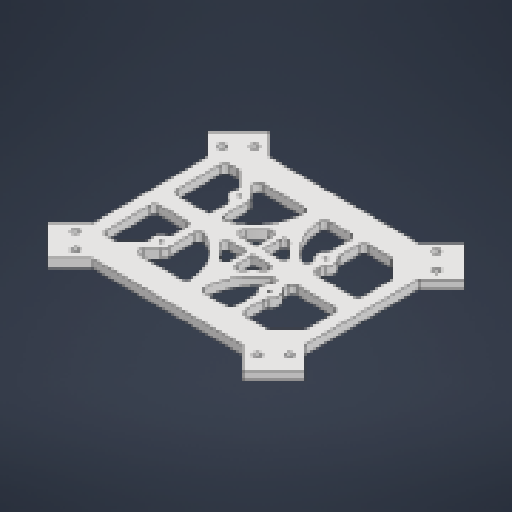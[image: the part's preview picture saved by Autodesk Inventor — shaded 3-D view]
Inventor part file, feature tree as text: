
AUTODESK INVENTOR PART (.ipt)
format: ipt  version: 2023 (Build 270158000, 158)  size: 514,048 bytes
history: native  units: in
note: dims shown in document units (in); Inventor stores cm internally (conversion verified against a paired STEP export)
features: extrude x2, fillet x1, sketch x1
ambient origin geometry x8: Origin, YZ Plane, XZ Plane, XY Plane, X Axis, Y Axis, Z Axis, Center Point
bodies: Solid1 (feature_tree)
feature tree (4):
  extrude  "Extrusion1"  Depth=0.25in TaperAngle=0.0deg
  extrude  "Extrusion12"  Depth=0.25in
  fillet  "Fillet2"  Radius=0.65in
  sketch  "Sketch11"  dims[d0=6.0in d2=0.25in d3=0.0in d44=0.25in d93=0.65in d96=0.6in d97=0.6in d103=0.5in d104=0.5in d105=0.5in d106=0.5in d108=0.625in d109=0.625in d121=1.0in d122=1.0in d123=1.5in d127=0.125in d130=0.125in d131=135.0deg d133=0.25in d138=0.6875in d139=0.0in d141=0.125in d146=0.0in d147=0.25in d150=0.25in d151=0.125in d152=45.0deg d153=0.75in d154=0.125in d156=0.2498in d157=0.25in d159=1.0in d160=1.0in d161=1.5in d164=0.2736in d165=0.75in d166=0.125in d167=0.0546in d168=0.25in d169=0.6661in d172=0.5in d174=0.25in d176=0.375in d177=0.375in d56=0.5in d57=0.0344in d58=0.5in d59=0.0344in d132=0.0344in d134=0.0344in]
